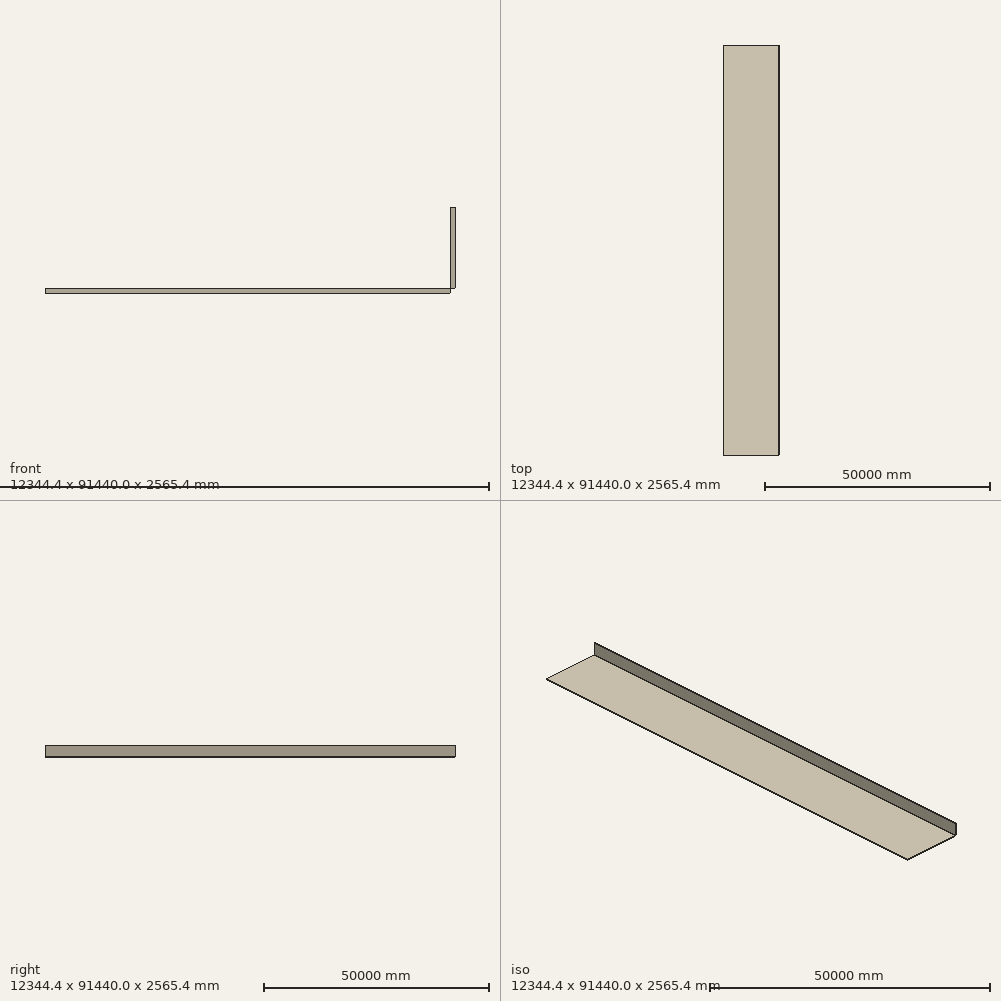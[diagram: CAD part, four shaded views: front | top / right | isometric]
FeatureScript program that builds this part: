
annotation { "Feature Type Name" : "Feature", "Feature Type Description" : "" }
export const myFeature = defineFeature(function(context is Context, id is Id, definition is map)
    precondition{}
    {
        {
            var Q0;
            Q0=qCreatedBy(makeId("Top.planeOp"),FACE);
            var sketch = newSketch(context, id + "F0", { "sketchPlane" : qUnion([Q0])});
            skLineSegment(sketch, "E0.bottom", {"start": v(6096, 45720) * mm, "end": v(-6096, 45720) * mm});
            skLineSegment(sketch, "E0.top", {"start": v(6096, -45720) * mm, "end": v(-6096, -45720) * mm});
            skLineSegment(sketch, "E0.left", {"start": v(6096, 45720) * mm, "end": v(6096, -45720) * mm});
            skLineSegment(sketch, "E0.right", {"start": v(-6096, 45720) * mm, "end": v(-6096, -45720) * mm});
            skPoint(sketch, "E0.middle", {"position": v(0, 0) * mm});
            skLineSegment(sketch, "E1.0", {"start": v(6248.4, 45720) * mm, "end": v(6248.4, -45720) * mm});
            skLineSegment(sketch, "E2", {"start": v(6096, 45720) * mm, "end": v(6248.4, 45720) * mm});
            skLineSegment(sketch, "E3", {"start": v(6096, -45720) * mm, "end": v(6248.4, -45720) * mm});
            skSolve(sketch);
        }
        {
            var Q0;
            Q0 = qSketchRegion(id + "F0", true);
            var sketch = newSketch(context, id + "F1", { "sketchPlane" : qUnion([Q0])});
            skPoint(sketch, "E4", {"position": v(6096, -39624) * mm});
            skLineSegment(sketch, "E5", {"start": v(6096, -39624) * mm, "end": v(-6096, -39624) * mm});
            skPoint(sketch, "E6", {"position": v(6096, 27432) * mm});
            skLineSegment(sketch, "E7", {"start": v(6096, 27432) * mm, "end": v(-6096, 27432) * mm});
            skSolve(sketch);
        }
        {
            var Q0;
            Q0=qCreatedBy(makeId("Top.planeOp"),FACE);
            var sketch = newSketch(context, id + "F2", { "sketchPlane" : qUnion([Q0])});
            skPoint(sketch, "E8", {"position": v(6096, 24993.6) * mm});
            skPoint(sketch, "E9", {"position": v(6096, 22555.2) * mm});
            skPoint(sketch, "E10", {"position": v(6096, 20116.8) * mm});
            skPoint(sketch, "E11", {"position": v(6096, 17678.4) * mm});
            skPoint(sketch, "E12", {"position": v(6096, 15240) * mm});
            skPoint(sketch, "E13", {"position": v(6096, 7924.8) * mm});
            skPoint(sketch, "E14", {"position": v(6096, 5486.4) * mm});
            skPoint(sketch, "E15", {"position": v(6096, 12801.6) * mm});
            skPoint(sketch, "E16", {"position": v(6096, 10363.2) * mm});
            skPoint(sketch, "E17", {"position": v(6096, 3048) * mm});
            skPoint(sketch, "E18", {"position": v(6096, 609.6) * mm});
            skPoint(sketch, "E19", {"position": v(6096, -1828.8) * mm});
            skPoint(sketch, "E20", {"position": v(6096, -4267.2) * mm});
            skPoint(sketch, "E21", {"position": v(6096, -6705.6) * mm});
            skPoint(sketch, "E22", {"position": v(6096, -9144) * mm});
            skPoint(sketch, "E23", {"position": v(6096, -11582.4) * mm});
            skPoint(sketch, "E24", {"position": v(6096, -14020.8) * mm});
            skPoint(sketch, "E25", {"position": v(6096, -16459.2) * mm});
            skPoint(sketch, "E26", {"position": v(6096, -18897.6) * mm});
            skPoint(sketch, "E27", {"position": v(6096, -21336) * mm});
            skPoint(sketch, "E28", {"position": v(6096, -23774.4) * mm});
            skPoint(sketch, "E29", {"position": v(6096, -26212.8) * mm});
            skPoint(sketch, "E30", {"position": v(6096, -28651.2) * mm});
            skPoint(sketch, "E31", {"position": v(6096, -31089.6) * mm});
            skPoint(sketch, "E32", {"position": v(6096, -33528) * mm});
            skPoint(sketch, "E33", {"position": v(6096, -35966.4) * mm});
            skPoint(sketch, "E34", {"position": v(6096, -38404.8) * mm});
            skPoint(sketch, "E35", {"position": v(6096, 27432) * mm});
            skSolve(sketch);
        }
        {
            var Q0;
            Q0=makeQuery(id+"F0.imprint","IMPRINT",FACE,{"disambiguationData":[TD([[makeQuery(id+"F0.imprint","IMPRINT",EDGE,{"derivedFrom":sQuery(id+"F0.wireOp",EDGE,"E0.bottom")}),1.0]])]});
            extrude(context, id + "F3", {"entities" : qUnion([Q0]), "oppositeDirection" : true, "depth" : 127 * mm});
        }
        {
            var Q0;
            Q0=makeQuery(id+"F0.imprint","IMPRINT",FACE,{"disambiguationData":[TD([[makeQuery(id+"F0.imprint","IMPRINT",EDGE,{"derivedFrom":sQuery(id+"F0.wireOp",EDGE,"E0.left")}),1.0]])]});
            extrude(context, id + "F4", {"entities" : qUnion([Q0]), "operationType" : NewBodyOperationType.ADD, "depth" : 2438.4 * mm});
        }
    });
